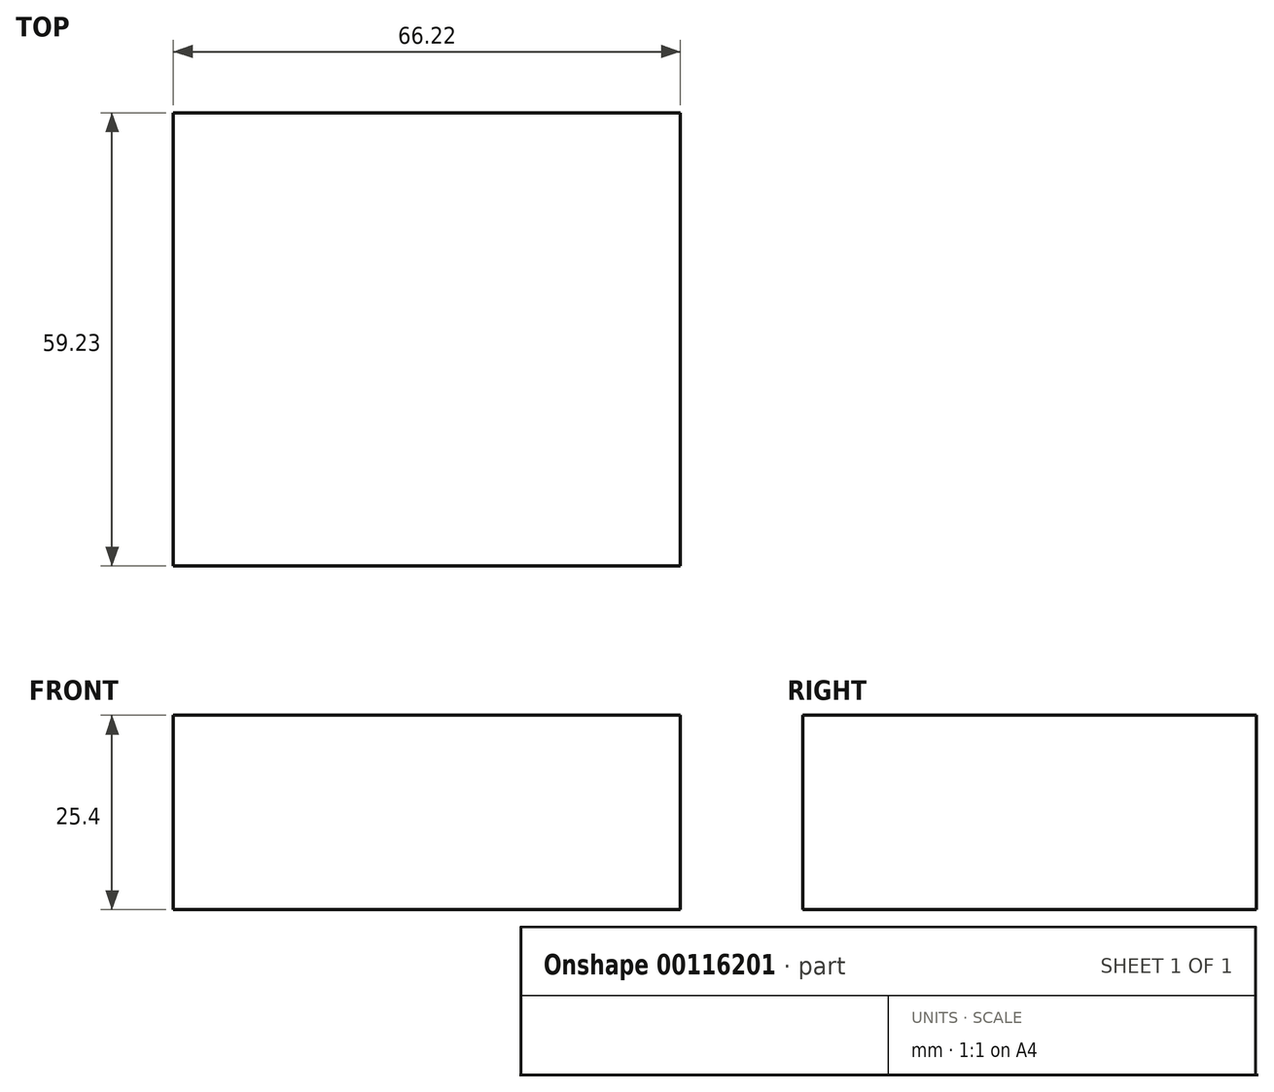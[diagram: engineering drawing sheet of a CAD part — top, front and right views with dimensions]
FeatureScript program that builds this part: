
annotation { "Feature Type Name" : "Feature", "Feature Type Description" : "" }
export const myFeature = defineFeature(function(context is Context, id is Id, definition is map)
    precondition{}
    {
        {
            var Q0;
            Q0=qCreatedBy(makeId("Top.planeOp"),FACE);
            var sketch = newSketch(context, id + "F0", { "sketchPlane" : qUnion([Q0])});
            skLineSegment(sketch, "E0.bottom", {"start": v(-67.2, 69.33) * mm, "end": v(-0.97, 69.33) * mm});
            skLineSegment(sketch, "E0.top", {"start": v(-67.2, 10.1) * mm, "end": v(-0.97, 10.1) * mm});
            skLineSegment(sketch, "E0.left", {"start": v(-67.2, 69.33) * mm, "end": v(-67.2, 10.1) * mm});
            skLineSegment(sketch, "E0.right", {"start": v(-0.97, 69.33) * mm, "end": v(-0.97, 10.1) * mm});
            skSolve(sketch);
        }
        {
            var Q0;
            Q0=makeQuery(id+"F0.imprint","IMPRINT",FACE,{"disambiguationData":[TD([[makeQuery(id+"F0.imprint","IMPRINT",EDGE,{"derivedFrom":sQuery(id+"F0.wireOp",EDGE,"E0.bottom")}),-1.0]])]});
            extrude(context, id + "F1", {"entities" : qUnion([Q0]), "depth" : 25.4 * mm});
        }
    });
